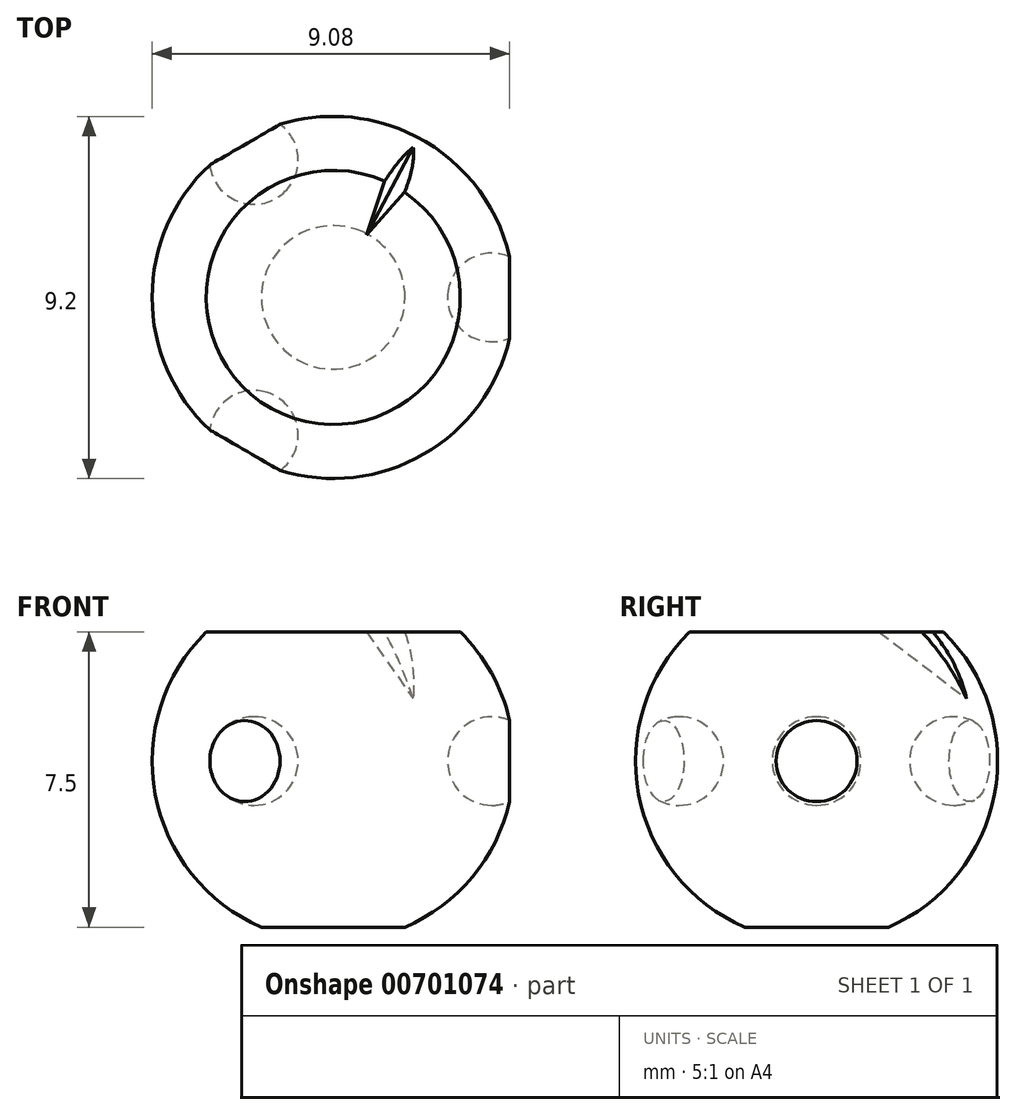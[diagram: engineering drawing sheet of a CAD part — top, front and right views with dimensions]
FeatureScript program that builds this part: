
annotation { "Feature Type Name" : "Feature", "Feature Type Description" : "" }
export const myFeature = defineFeature(function(context is Context, id is Id, definition is map)
    precondition{}
    {
        {
            var Q0;
            Q0=qCreatedBy(makeId("Front.planeOp"),FACE);
            var sketch = newSketch(context, id + "F0", { "sketchPlane" : qUnion([Q0])});
            skArc(sketch, "E0", {"start": v(0, -4.6) * mm, "mid": v(4.6, 0) * mm, "end": v(0, 4.6) * mm});
            skLineSegment(sketch, "E1", {"start": v(0, 4.6) * mm, "end": v(0, -4.6) * mm});
            skSolve(sketch);
        }
        {
            var Q0;
            Q0=makeQuery(id+"F0.imprint","IMPRINT",FACE,{"disambiguationData":[TD([[makeQuery(id+"F0.imprint","IMPRINT",EDGE,{"derivedFrom":sQuery(id+"F0.wireOp",EDGE,"E0")}),1.0]])]});
            var Q1;
            Q1=sQuery(id+"F0.wireOp",EDGE,"E1");
            revolve(context, id + "F1", {"entities" : qUnion([Q0]), "axis" : qUnion([Q1]), "revolveType" : RevolveType.FULL});
        }
        {
            var Q0;
            Q0=qCreatedBy(makeId("Top.planeOp"),FACE);
            cPlane(context, id + "F2", {"entities" : qUnion([Q0]), "cplaneType" : CPlaneType.OFFSET, "offset" : 3.28 * mm, "width" : 152.4 * mm, "height" : 152.4 * mm});
        }
        {
            var Q0;
            Q0=qCreatedBy(makeId("Top.planeOp"),FACE);
            var Q1;
            Q1 = qBodyType(qCreatedBy(id + "F5" ,EDGE), BodyType.WIRE);
            cPlane(context, id + "F3", {"entities" : qUnion([Q0, Q1]), "cplaneType" : CPlaneType.OFFSET, "offset" : 4.22 * mm, "oppositeDirection" : true, "width" : 152.4 * mm, "height" : 152.4 * mm});
        }
        {
            var Q0;
            Q0=qCreatedBy(id+"F2.planeOp",FACE);
            var sketch = newSketch(context, id + "F4", { "sketchPlane" : qUnion([Q0])});
            skCircle(sketch, "E2", {"center": v(0, 0) * mm, "radius": 3.25 * mm});
            skSolve(sketch);
        }
        {
            var Q0;
            Q0=qCreatedBy(id+"F3.planeOp",FACE);
            var sketch = newSketch(context, id + "F5", { "sketchPlane" : qUnion([Q0])});
            skCircle(sketch, "E3", {"center": v(-3.46, 0) * mm, "radius": 13.27 * mm});
            skSolve(sketch);
        }
        {
            var Q0;
            Q0 = qSketchRegion(id + "F4", true);
            extrude(context, id + "F6", {"entities" : qUnion([Q0]), "operationType" : NewBodyOperationType.REMOVE, "depth" : 25.4 * mm, "offsetDistance" : 25.4 * mm});
        }
        {
            var Q0;
            Q0 = qSketchRegion(id + "F5", true);
            extrude(context, id + "F7", {"entities" : qUnion([Q0]), "operationType" : NewBodyOperationType.REMOVE, "oppositeDirection" : true, "depth" : 25.4 * mm, "offsetDistance" : 25.4 * mm});
        }
        {
            var Q0;
            Q0=qCreatedBy(makeId("Right.planeOp"),FACE);
            var Q1;
            Q1 = qBodyType(qCreatedBy(id + "F9" ,EDGE), BodyType.WIRE);
            cPlane(context, id + "F8", {"entities" : qUnion([Q0, Q1]), "cplaneType" : CPlaneType.OFFSET, "offset" : 4.03 * mm, "oppositeDirection" : true, "width" : 152.4 * mm, "height" : 152.4 * mm});
        }
        {
            var Q0;
            Q0=qCreatedBy(id+"F8.planeOp",FACE);
            var sketch = newSketch(context, id + "F9", { "sketchPlane" : qUnion([Q0])});
            skArc(sketch, "E4", {"start": v(0, -1.12) * mm, "mid": v(1.13, 0) * mm, "end": v(0, 1.13) * mm});
            skLineSegment(sketch, "E5", {"start": v(0, 1.13) * mm, "end": v(0, -1.12) * mm});
            skSolve(sketch);
        }
        {
            var Q0;
            Q0=qCreatedBy(makeId("Front.planeOp"),FACE);
            var sketch = newSketch(context, id + "F10", { "sketchPlane" : qUnion([Q0])});
            skLineSegment(sketch, "E6", {"start": v(0, 0) * mm, "end": v(0, 3.28) * mm});
            skLineSegment(sketch, "E7", {"start": v(0, 0) * mm, "end": v(0, -4.22) * mm});
            skSolve(sketch);
        }
        {
            var Q0;
            Q0=qCreatedBy(makeId("Front.planeOp"),FACE);
            cPlane(context, id + "F11", {"entities" : qUnion([Q0]), "cplaneType" : CPlaneType.OFFSET, "offset" : 4.03 * mm, "width" : 150 * mm, "height" : 150 * mm});
        }
        {
            var Q0;
            Q0=qCreatedBy(makeId("Front.planeOp"),FACE);
            cPlane(context, id + "F12", {"entities" : qUnion([Q0]), "cplaneType" : CPlaneType.OFFSET, "offset" : 4.03 * mm, "oppositeDirection" : true, "width" : 150 * mm, "height" : 150 * mm});
        }
        {
            var Q0;
            Q0=qCreatedBy(makeId("Right.planeOp"),FACE);
            cPlane(context, id + "F13", {"entities" : qUnion([Q0]), "cplaneType" : CPlaneType.OFFSET, "offset" : 4.03 * mm, "width" : 150 * mm, "height" : 150 * mm});
        }
        {
            var Q0;
            Q0=qCreatedBy(id+"F13.planeOp",FACE);
            var sketch = newSketch(context, id + "F14", { "sketchPlane" : qUnion([Q0])});
            skLineSegment(sketch, "E8", {"start": v(0, 0) * mm, "end": v(0, -1.12) * mm});
            skArc(sketch, "E9", {"start": v(0, -1.12) * mm, "mid": v(1.12, 0) * mm, "end": v(0, 1.12) * mm});
            skLineSegment(sketch, "E10", {"start": v(0, -1.12) * mm, "end": v(0, 1.12) * mm});
            skSolve(sketch);
        }
        {
            var Q0;
            Q0 = qSketchRegion(id + "F14", true);
            var Q1;
            Q1=sQuery(id+"F14.wireOp",EDGE,"E10");
            revolve(context, id + "F15", {"operationType" : NewBodyOperationType.REMOVE, "entities" : qUnion([Q0]), "axis" : qUnion([Q1]), "revolveType" : RevolveType.FULL});
        }
        {
            var Q0;
            Q0=sQuery(id+"F10.wireOp",EDGE,"E6");
            cPlane(context, id + "F16", {"entities" : qUnion([Q0]), "cplaneType" : CPlaneType.LINE_ANGLE, "offset" : 25 * mm, "angle" : 120 * degree, "width" : 150 * mm, "height" : 150 * mm});
        }
        {
            var Q0;
            Q0=qCreatedBy(id+"F16.planeOp",FACE);
            cPlane(context, id + "F17", {"entities" : qUnion([Q0]), "cplaneType" : CPlaneType.OFFSET, "offset" : 4.03 * mm, "width" : 150 * mm, "height" : 150 * mm});
        }
        {
            var Q0;
            Q0=qCreatedBy(id+"F17.planeOp",FACE);
            var sketch = newSketch(context, id + "F18", { "sketchPlane" : qUnion([Q0])});
            skLineSegment(sketch, "E11", {"start": v(0, 0) * mm, "end": v(0, -1.13) * mm});
            skArc(sketch, "E12", {"start": v(0, -1.12) * mm, "mid": v(1.12, 0) * mm, "end": v(0, 1.12) * mm});
            skLineSegment(sketch, "E13", {"start": v(0, -1.13) * mm, "end": v(0, 1.13) * mm});
            skSolve(sketch);
        }
        {
            var Q0;
            Q0 = qSketchRegion(id + "F18", true);
            var Q1;
            Q1=sQuery(id+"F18.wireOp",EDGE,"E13");
            revolve(context, id + "F19", {"operationType" : NewBodyOperationType.REMOVE, "surfaceOperationType" : NewSurfaceOperationType.NEW, "entities" : qUnion([Q0]), "axis" : qUnion([Q1]), "revolveType" : RevolveType.FULL, "oppositeDirection" : true});
        }
        {
            var Q0;
            Q0=sQuery(id+"F10.wireOp",EDGE,"E6");
            cPlane(context, id + "F20", {"entities" : qUnion([Q0]), "cplaneType" : CPlaneType.LINE_ANGLE, "offset" : 25 * mm, "angle" : 240 * degree, "width" : 150 * mm, "height" : 150 * mm});
        }
        {
            var Q0;
            Q0=qCreatedBy(id+"F20.planeOp",FACE);
            cPlane(context, id + "F21", {"entities" : qUnion([Q0]), "cplaneType" : CPlaneType.OFFSET, "offset" : 4.03 * mm, "width" : 150 * mm, "height" : 150 * mm});
        }
        {
            var Q0;
            Q0=qCreatedBy(id+"F21.planeOp",FACE);
            var sketch = newSketch(context, id + "F22", { "sketchPlane" : qUnion([Q0])});
            skLineSegment(sketch, "E14", {"start": v(0, 0) * mm, "end": v(0, -1.13) * mm});
            skArc(sketch, "E15", {"start": v(0, -1.12) * mm, "mid": v(1.12, 0) * mm, "end": v(0, 1.12) * mm});
            skLineSegment(sketch, "E16", {"start": v(0, -1.13) * mm, "end": v(0, 1.13) * mm});
            skSolve(sketch);
        }
        {
            var Q0;
            Q0 = qSketchRegion(id + "F22", true);
            var Q1;
            Q1=sQuery(id+"F22.wireOp",EDGE,"E16");
            revolve(context, id + "F23", {"operationType" : NewBodyOperationType.REMOVE, "surfaceOperationType" : NewSurfaceOperationType.NEW, "entities" : qUnion([Q0]), "axis" : qUnion([Q1]), "revolveType" : RevolveType.FULL, "oppositeDirection" : true});
        }
        {
            var Q0;
            Q0=sQuery(id+"F10.wireOp",EDGE,"E6");
            cPlane(context, id + "F24", {"entities" : qUnion([Q0]), "cplaneType" : CPlaneType.LINE_ANGLE, "offset" : 25 * mm, "angle" : 45 * degree, "width" : 150 * mm, "height" : 150 * mm});
        }
        {
            var Q0;
            Q0=qCreatedBy(id+"F24.planeOp",FACE);
            cPlane(context, id + "F25", {"entities" : qUnion([Q0]), "cplaneType" : CPlaneType.OFFSET, "offset" : 4.03 * mm, "width" : 150 * mm, "height" : 150 * mm});
        }
        {
            var Q0;
            Q0=qCreatedBy(id+"F25.planeOp",FACE);
            var sketch = newSketch(context, id + "F26", { "sketchPlane" : qUnion([Q0])});
            skLineSegment(sketch, "E17", {"start": v(0, 3.4) * mm, "end": v(0, 2.48) * mm});
            skLineSegment(sketch, "E18", {"start": v(0, 2.48) * mm, "end": v(0.34, 3.39) * mm});
            skLineSegment(sketch, "E19", {"start": v(0, 2.48) * mm, "end": v(-0.42, 3.4) * mm});
            skLineSegment(sketch, "E20", {"start": v(-0.42, 3.4) * mm, "end": v(0.34, 3.39) * mm});
            skLineSegment(sketch, "E21", {"start": v(-0.86, 1.83) * mm, "end": v(0.93, 1.83) * mm});
            skLineSegment(sketch, "E22", {"start": v(0, 2.48) * mm, "end": v(0, 1.4) * mm});
            skSolve(sketch);
        }
        {
            var Q0;
            Q0=sQuery(id+"F26.wireOp",EDGE,"E21");
            cPlane(context, id + "F27", {"entities" : qUnion([Q0]), "cplaneType" : CPlaneType.LINE_ANGLE, "offset" : 25 * mm, "angle" : 35 * degree, "width" : 150 * mm, "height" : 150 * mm});
        }
        {
            var Q0;
            Q0=qCreatedBy(id+"F27.planeOp",FACE);
            var sketch = newSketch(context, id + "F28", { "sketchPlane" : qUnion([Q0])});
            skLineSegment(sketch, "E23", {"start": v(1.2, 4.25) * mm, "end": v(0.69, 3.15) * mm});
            skSolve(sketch);
        }
        {
            var Q0;
            Q0=sQuery(id+"F28.wireOp",VERTEX,"E23.start");
            var Q1;
            Q1=sQuery(id+"F28.wireOp",EDGE,"E23");
            cPlane(context, id + "F29", {"entities" : qUnion([Q0, Q1]), "cplaneType" : CPlaneType.LINE_POINT, "offset" : 25 * mm, "width" : 150 * mm, "height" : 150 * mm});
        }
        {
            var Q0;
            Q0=qCreatedBy(id+"F29.planeOp",FACE);
            var sketch = newSketch(context, id + "F30", { "sketchPlane" : qUnion([Q0])});
            skLineSegment(sketch, "E24", {"start": v(1.88, 4.54) * mm, "end": v(1.06, 4.86) * mm});
            skLineSegment(sketch, "E25", {"start": v(1.06, 4.86) * mm, "end": v(1.06, 3.57) * mm});
            skLineSegment(sketch, "E26", {"start": v(1.06, 3.57) * mm, "end": v(1.88, 4.54) * mm});
            skSolve(sketch);
        }
        {
            var Q0;
            Q0=makeQuery(id+"F30.imprint","IMPRINT",FACE,{"disambiguationData":[TD([[makeQuery(id+"F30.imprint","IMPRINT",EDGE,{"derivedFrom":sQuery(id+"F30.wireOp",EDGE,"E24")}),1.0]])]});
            extrude(context, id + "F31", {"entities" : qUnion([Q0]), "operationType" : NewBodyOperationType.REMOVE, "depth" : 18.5 * mm, "offsetDistance" : 25 * mm});
        }
    });
